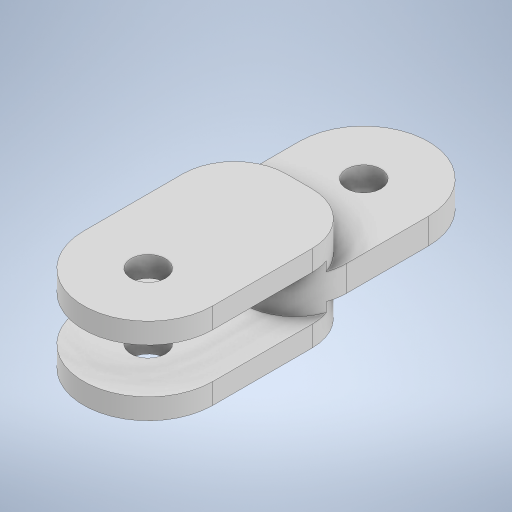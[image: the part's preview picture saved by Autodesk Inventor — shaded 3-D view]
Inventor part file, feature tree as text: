
AUTODESK INVENTOR PART (.ipt)
format: ipt  version: 2024.2 (Build 282272000, 272)  size: 289,280 bytes
history: native  units: mm
features: extrude x3, sketch x3, fillet x2
ambient origin geometry x8: Origin, YZ Plane, XZ Plane, XY Plane, X Axis, Y Axis, Z Axis, Center Point
bodies: Solid1 (feature_tree)
feature tree (8):
  extrude  "Extrusion1"  Depth=15.0mm
  extrude  "Extrusion2"  Depth=10.0mm
  fillet  "Fillet1"  Radius=10.0mm
  extrude  "Extrusion4"  Depth=5.2mm
  fillet  "Fillet2"  [1 undecoded]
  sketch  "Sketch1"  dims[d0=15.0mm d2=25.0mm]
  sketch  "Sketch2"  dims[d3=4.0mm d4=4.0mm d5=10.0mm d6=0.0mm]
  sketch  "Sketch4"  dims[d7=17.0mm d8=5.2mm d9=0.0mm d10=0.0mm d11=6.0mm d15=3.0mm d16=15.0mm d17=0.0mm d18=0.0mm d19=6.0mm]
note: 1 required parameter value undecoded (feature->parameter linkage not recoverable at this tier; creation-order binding heuristic only, values carry confidence <= 0.55)
